# Revit family: Equipment-Gym-Draper_Inc.-Rear_Folding_Backstop-TB-25R
name_source: partatom
category: Specialty Equipment
revit_build: Autodesk Revit Architecture 2012 (Build: 20110309_2315(x64)
units: mm (PartAtom-declared; Revit-internal decimal feet)

## types (11) — shared parameters
Apparent Load = 746 VA
Backboard Frame = Metal - Draper Inc. - Aluminum
Backboard Length = 6' - 0"
C = 11 1/4"
Constraint C = 11 1/4"
Description = Basketball Backstop
Frame = Metal - Draper Inc. - White Paint
Frequency = 60 Hz
Manufacturer = Draper Inc.
Model = TB-25R
Number of Poles = 1
Power Factor = 1
Product Documentation Link = http://www.draperinc.com
Product Name = Rear Folding Basketball Backstops
Product Page URL = http://www.draperinc.com
URL = http://www.draperinc.com
Voltage = 120 V

## per-type parameters (varying)
| type | Backboard Height | Backstop | Fan Backstop | Rect Backstop | Stripe |
| 503152 72"x48" Rect. Glass | 4' - 0" | Glass - Draper Inc. - Backboard Glass | No | Yes | Metal - Draper Inc. - White Paint |
| 503136 72''x48'' Rect. Glass | 4' - 0" | Glass - Draper Inc. - Backboard Glass | No | Yes | Metal - Draper Inc. - White Paint |
| 503151 72''x48'' Rect. Wood | 4' - 0" | Wood - Draper Inc. - White Paint | No | Yes | Paintl - Draper Inc. - Red Paint |
| 503140 72''x42'' Rect. Wood | 3' - 6" | Wood - Draper Inc. - White Paint | No | Yes | Paintl - Draper Inc. - Red Paint |
| 503153 72''x48'' Rect. Fiberglass | 4' - 0" | Plastic - Draper Inc. - Fiberglass - White | No | Yes | Paintl - Draper Inc. - Red Paint |
| 503144 72" x 42" Rect. Fiberglass | 3' - 6" | Plastic - Draper Inc. - Fiberglass - White | No | Yes | Paintl - Draper Inc. - Red Paint |
| 503154 72" x 48" Rectangular Steel | 4' - 0" | Metal - Draper Inc. - Steel - White Paint | No | Yes | Paintl - Draper Inc. - Red Paint |
| 503167 72" x 42" Rectangular Steel | 3' - 6" | Metal - Draper Inc. - Steel - White Paint | No | Yes | Paintl - Draper Inc. - Red Paint |
| 503150 Fan Glass | 4' - 0" | Glass - Draper Inc. - Backboard Glass | Yes | No | Metal - Draper Inc. - White Paint |
| 503148 Fan Fiberglass | 4' - 0" | Plastic - Draper Inc. - Fiberglass - White | Yes | No | Paintl - Draper Inc. - Red Paint |
| 503143 Fan Aluminum | 4' - 0" | Metal - Draper Inc. - Aluminum - White Paint | Yes | No | Paintl - Draper Inc. - Red Paint |

## geometry (parser evidence)
native form markers: Blend x6, Sweep x11
no freeform markers — native parametric forms only
